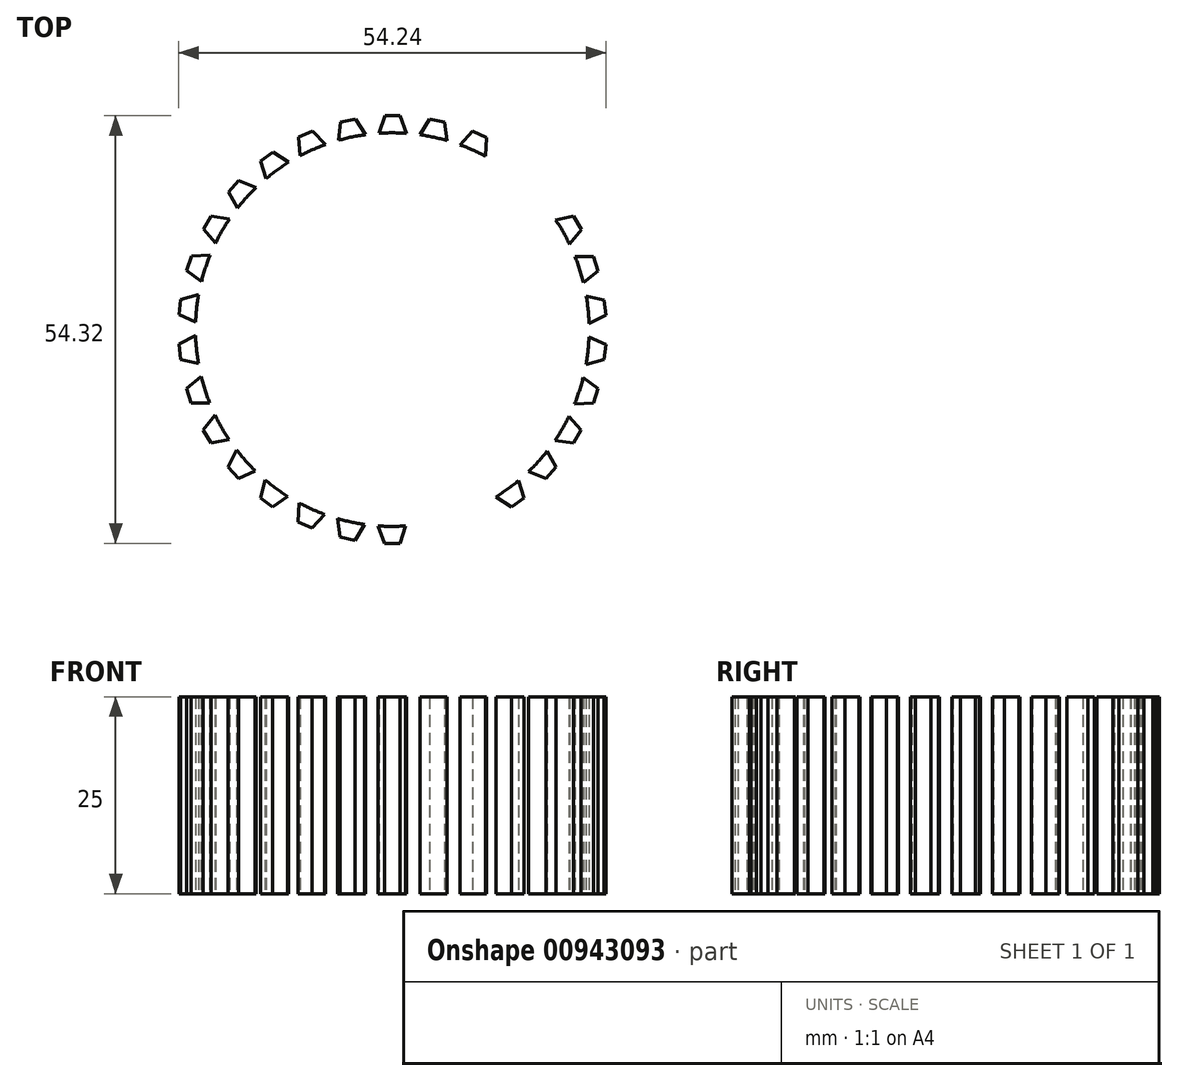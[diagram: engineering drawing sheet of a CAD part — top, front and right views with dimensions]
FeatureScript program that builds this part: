
annotation { "Feature Type Name" : "Feature", "Feature Type Description" : "" }
export const myFeature = defineFeature(function(context is Context, id is Id, definition is map)
    precondition{}
    {
        {
            var Q0;
            Q0=qCreatedBy(makeId("Top.planeOp"),FACE);
            var sketch = newSketch(context, id + "F0", { "sketchPlane" : qUnion([Q0])});
            skCircle(sketch, "E0", {"center": v(0, 0) * mm, "radius": 25 * mm});
            skLineSegment(sketch, "E1", {"start": v(0, 0) * mm, "end": v(0, 25) * mm});
            skLineSegment(sketch, "E2", {"start": v(-1.69, 24.94) * mm, "end": v(-0.95, 27.16) * mm});
            skLineSegment(sketch, "E3", {"start": v(-0.95, 27.16) * mm, "end": v(0.98, 27.16) * mm});
            skLineSegment(sketch, "E4", {"start": v(0.98, 27.16) * mm, "end": v(1.84, 24.93) * mm});
            skLineSegment(sketch, "E5.1.0", {"start": v(-6.83, 24.05) * mm, "end": v(-6.58, 26.37) * mm});
            skLineSegment(sketch, "E5.1.1", {"start": v(-6.58, 26.37) * mm, "end": v(-4.68, 26.77) * mm});
            skLineSegment(sketch, "E5.1.2", {"start": v(-4.68, 26.77) * mm, "end": v(-3.39, 24.77) * mm});
            skLineSegment(sketch, "E5.2.0", {"start": v(-11.69, 22.1) * mm, "end": v(-11.92, 24.43) * mm});
            skLineSegment(sketch, "E5.2.1", {"start": v(-11.92, 24.43) * mm, "end": v(-10.15, 25.21) * mm});
            skLineSegment(sketch, "E5.2.2", {"start": v(-10.15, 25.21) * mm, "end": v(-8.46, 23.52) * mm});
            skLineSegment(sketch, "E5.3.0", {"start": v(-16.02, 19.19) * mm, "end": v(-16.74, 21.41) * mm});
            skLineSegment(sketch, "E5.3.1", {"start": v(-16.74, 21.41) * mm, "end": v(-15.17, 22.55) * mm});
            skLineSegment(sketch, "E5.3.2", {"start": v(-15.17, 22.55) * mm, "end": v(-13.17, 21.25) * mm});
            skLineSegment(sketch, "E5.4.0", {"start": v(-19.66, 15.44) * mm, "end": v(-20.82, 17.47) * mm});
            skLineSegment(sketch, "E5.4.1", {"start": v(-20.82, 17.47) * mm, "end": v(-19.53, 18.9) * mm});
            skLineSegment(sketch, "E5.4.2", {"start": v(-19.53, 18.9) * mm, "end": v(-17.3, 18.05) * mm});
            skLineSegment(sketch, "E5.5.0", {"start": v(-22.44, 11.01) * mm, "end": v(-24, 12.76) * mm});
            skLineSegment(sketch, "E5.5.1", {"start": v(-24, 12.76) * mm, "end": v(-23.03, 14.43) * mm});
            skLineSegment(sketch, "E5.5.2", {"start": v(-23.03, 14.43) * mm, "end": v(-20.67, 14.06) * mm});
            skLineSegment(sketch, "E5.6.0", {"start": v(-24.24, 6.1) * mm, "end": v(-26.13, 7.49) * mm});
            skLineSegment(sketch, "E5.6.1", {"start": v(-26.13, 7.49) * mm, "end": v(-25.53, 9.33) * mm});
            skLineSegment(sketch, "E5.6.2", {"start": v(-25.53, 9.33) * mm, "end": v(-23.14, 9.45) * mm});
            skLineSegment(sketch, "E5.7.0", {"start": v(-24.98, 0.93) * mm, "end": v(-27.11, 1.9) * mm});
            skLineSegment(sketch, "E5.7.1", {"start": v(-27.11, 1.9) * mm, "end": v(-26.91, 3.82) * mm});
            skLineSegment(sketch, "E5.7.2", {"start": v(-26.91, 3.82) * mm, "end": v(-24.6, 4.43) * mm});
            skLineSegment(sketch, "E5.8.0", {"start": v(-24.63, -4.28) * mm, "end": v(-26.91, -3.79) * mm});
            skLineSegment(sketch, "E5.8.1", {"start": v(-26.91, -3.79) * mm, "end": v(-27.12, -1.86) * mm});
            skLineSegment(sketch, "E5.8.2", {"start": v(-27.12, -1.86) * mm, "end": v(-24.99, -0.78) * mm});
            skLineSegment(sketch, "E5.9.0", {"start": v(-23.2, -9.31) * mm, "end": v(-25.54, -9.3) * mm});
            skLineSegment(sketch, "E5.9.1", {"start": v(-25.54, -9.3) * mm, "end": v(-26.14, -7.46) * mm});
            skLineSegment(sketch, "E5.9.2", {"start": v(-26.14, -7.46) * mm, "end": v(-24.28, -5.96) * mm});
            skLineSegment(sketch, "E5.10.0", {"start": v(-20.76, -13.93) * mm, "end": v(-23.05, -14.4) * mm});
            skLineSegment(sketch, "E5.10.1", {"start": v(-23.05, -14.4) * mm, "end": v(-24.02, -12.73) * mm});
            skLineSegment(sketch, "E5.10.2", {"start": v(-24.02, -12.73) * mm, "end": v(-22.51, -10.87) * mm});
            skLineSegment(sketch, "E5.11.0", {"start": v(-17.4, -17.94) * mm, "end": v(-19.55, -18.88) * mm});
            skLineSegment(sketch, "E5.11.1", {"start": v(-19.55, -18.88) * mm, "end": v(-20.84, -17.44) * mm});
            skLineSegment(sketch, "E5.11.2", {"start": v(-20.84, -17.44) * mm, "end": v(-19.76, -15.32) * mm});
            skLineSegment(sketch, "E5.12.0", {"start": v(-13.3, -21.17) * mm, "end": v(-15.2, -22.53) * mm});
            skLineSegment(sketch, "E5.12.1", {"start": v(-15.2, -22.53) * mm, "end": v(-16.76, -21.4) * mm});
            skLineSegment(sketch, "E5.12.2", {"start": v(-16.76, -21.4) * mm, "end": v(-16.14, -19.1) * mm});
            skLineSegment(sketch, "E5.13.0", {"start": v(-8.6, -23.47) * mm, "end": v(-10.18, -25.2) * mm});
            skLineSegment(sketch, "E5.13.1", {"start": v(-10.18, -25.2) * mm, "end": v(-11.95, -24.41) * mm});
            skLineSegment(sketch, "E5.13.2", {"start": v(-11.95, -24.41) * mm, "end": v(-11.82, -22.03) * mm});
            skLineSegment(sketch, "E5.14.0", {"start": v(-3.54, -24.75) * mm, "end": v(-4.72, -26.77) * mm});
            skLineSegment(sketch, "E5.14.1", {"start": v(-4.72, -26.77) * mm, "end": v(-6.61, -26.36) * mm});
            skLineSegment(sketch, "E5.14.2", {"start": v(-6.61, -26.36) * mm, "end": v(-6.98, -24) * mm});
            skLineSegment(sketch, "E5.15.0", {"start": v(1.69, -24.94) * mm, "end": v(0.95, -27.16) * mm});
            skLineSegment(sketch, "E5.15.1", {"start": v(0.95, -27.16) * mm, "end": v(-0.98, -27.16) * mm});
            skLineSegment(sketch, "E5.15.2", {"start": v(-0.98, -27.16) * mm, "end": v(-1.84, -24.93) * mm});
            skLineSegment(sketch, "E5.16.0", {"start": v(6.83, -24.05) * mm, "end": v(6.58, -26.37) * mm});
            skLineSegment(sketch, "E5.16.1", {"start": v(6.58, -26.37) * mm, "end": v(4.68, -26.77) * mm});
            skLineSegment(sketch, "E5.16.2", {"start": v(4.68, -26.77) * mm, "end": v(3.39, -24.77) * mm});
            skLineSegment(sketch, "E5.17.0", {"start": v(11.69, -22.1) * mm, "end": v(11.92, -24.43) * mm});
            skLineSegment(sketch, "E5.17.1", {"start": v(11.92, -24.43) * mm, "end": v(10.15, -25.21) * mm});
            skLineSegment(sketch, "E5.17.2", {"start": v(10.15, -25.21) * mm, "end": v(8.46, -23.52) * mm});
            skLineSegment(sketch, "E5.18.0", {"start": v(16.02, -19.19) * mm, "end": v(16.74, -21.41) * mm});
            skLineSegment(sketch, "E5.18.1", {"start": v(16.74, -21.41) * mm, "end": v(15.17, -22.55) * mm});
            skLineSegment(sketch, "E5.18.2", {"start": v(15.17, -22.55) * mm, "end": v(13.17, -21.25) * mm});
            skLineSegment(sketch, "E5.19.0", {"start": v(19.66, -15.44) * mm, "end": v(20.82, -17.47) * mm});
            skLineSegment(sketch, "E5.19.1", {"start": v(20.82, -17.47) * mm, "end": v(19.53, -18.9) * mm});
            skLineSegment(sketch, "E5.19.2", {"start": v(19.53, -18.9) * mm, "end": v(17.3, -18.05) * mm});
            skLineSegment(sketch, "E5.20.0", {"start": v(22.44, -11.01) * mm, "end": v(24, -12.76) * mm});
            skLineSegment(sketch, "E5.20.1", {"start": v(24, -12.76) * mm, "end": v(23.03, -14.43) * mm});
            skLineSegment(sketch, "E5.20.2", {"start": v(23.03, -14.43) * mm, "end": v(20.67, -14.06) * mm});
            skLineSegment(sketch, "E5.21.0", {"start": v(24.24, -6.1) * mm, "end": v(26.13, -7.49) * mm});
            skLineSegment(sketch, "E5.21.1", {"start": v(26.13, -7.49) * mm, "end": v(25.53, -9.33) * mm});
            skLineSegment(sketch, "E5.21.2", {"start": v(25.53, -9.33) * mm, "end": v(23.14, -9.45) * mm});
            skLineSegment(sketch, "E5.22.0", {"start": v(24.98, -0.93) * mm, "end": v(27.11, -1.9) * mm});
            skLineSegment(sketch, "E5.22.1", {"start": v(27.11, -1.9) * mm, "end": v(26.91, -3.82) * mm});
            skLineSegment(sketch, "E5.22.2", {"start": v(26.91, -3.82) * mm, "end": v(24.6, -4.43) * mm});
            skLineSegment(sketch, "E5.23.0", {"start": v(24.63, 4.28) * mm, "end": v(26.91, 3.79) * mm});
            skLineSegment(sketch, "E5.23.1", {"start": v(26.91, 3.79) * mm, "end": v(27.12, 1.86) * mm});
            skLineSegment(sketch, "E5.23.2", {"start": v(27.12, 1.86) * mm, "end": v(24.99, 0.78) * mm});
            skLineSegment(sketch, "E5.24.0", {"start": v(23.2, 9.31) * mm, "end": v(25.54, 9.3) * mm});
            skLineSegment(sketch, "E5.24.1", {"start": v(25.54, 9.3) * mm, "end": v(26.14, 7.46) * mm});
            skLineSegment(sketch, "E5.24.2", {"start": v(26.14, 7.46) * mm, "end": v(24.28, 5.96) * mm});
            skLineSegment(sketch, "E5.25.0", {"start": v(20.76, 13.93) * mm, "end": v(23.05, 14.4) * mm});
            skLineSegment(sketch, "E5.25.1", {"start": v(23.05, 14.4) * mm, "end": v(24.02, 12.73) * mm});
            skLineSegment(sketch, "E5.25.2", {"start": v(24.02, 12.73) * mm, "end": v(22.51, 10.87) * mm});
            skLineSegment(sketch, "E5.26.0", {"start": v(17.4, 17.94) * mm, "end": v(19.55, 18.88) * mm});
            skLineSegment(sketch, "E5.26.1", {"start": v(19.55, 18.88) * mm, "end": v(20.84, 17.44) * mm});
            skLineSegment(sketch, "E5.26.2", {"start": v(20.84, 17.44) * mm, "end": v(19.76, 15.32) * mm});
            skLineSegment(sketch, "E5.27.0", {"start": v(13.3, 21.17) * mm, "end": v(15.2, 22.53) * mm});
            skLineSegment(sketch, "E5.27.1", {"start": v(15.2, 22.53) * mm, "end": v(16.76, 21.4) * mm});
            skLineSegment(sketch, "E5.27.2", {"start": v(16.76, 21.4) * mm, "end": v(16.14, 19.1) * mm});
            skLineSegment(sketch, "E5.28.0", {"start": v(8.6, 23.47) * mm, "end": v(10.18, 25.2) * mm});
            skLineSegment(sketch, "E5.28.1", {"start": v(10.18, 25.2) * mm, "end": v(11.95, 24.41) * mm});
            skLineSegment(sketch, "E5.28.2", {"start": v(11.95, 24.41) * mm, "end": v(11.82, 22.03) * mm});
            skLineSegment(sketch, "E5.29.0", {"start": v(3.54, 24.75) * mm, "end": v(4.72, 26.77) * mm});
            skLineSegment(sketch, "E5.29.1", {"start": v(4.72, 26.77) * mm, "end": v(6.61, 26.36) * mm});
            skLineSegment(sketch, "E5.29.2", {"start": v(6.61, 26.36) * mm, "end": v(6.98, 24) * mm});
            skSolve(sketch);
        }
        {
            var Q0;
            {var subQ0=sQuery(id+"F0.wireOp",EDGE,"E0");var subQ56=makeQuery(id+"F0.imprint","IMPRINT",VERTEX,{"derivedFrom":subQ0});Q0=makeQuery(id+"F0.imprint","IMPRINT",FACE,{"disambiguationData":[TD([[makeQuery(id+"F0.imprint","IMPRINT",EDGE,{"disambiguationData":[TD([[subQ56,1.0]])],"derivedFrom":subQ0}),-1.0]])]});}
            var Q1;
            {var subQ3=sQuery(id+"F0.wireOp",EDGE,"E2");Q1=makeQuery(id+"F0.imprint","IMPRINT",FACE,{"disambiguationData":[TD([[makeQuery(id+"F0.imprint","IMPRINT",EDGE,{"derivedFrom":subQ3}),-1.0]])]});}
            var Q2;
            {var subQ0=sQuery(id+"F0.wireOp",EDGE,"E5.19.0");Q2=makeQuery(id+"F0.imprint","IMPRINT",FACE,{"disambiguationData":[TD([[makeQuery(id+"F0.imprint","IMPRINT",EDGE,{"derivedFrom":subQ0}),-1.0]])]});}
            var Q3;
            {var subQ0=sQuery(id+"F0.wireOp",EDGE,"E5.21.0");Q3=makeQuery(id+"F0.imprint","IMPRINT",FACE,{"disambiguationData":[TD([[makeQuery(id+"F0.imprint","IMPRINT",EDGE,{"derivedFrom":subQ0}),-1.0]])]});}
            var Q4;
            {var subQ0=sQuery(id+"F0.wireOp",EDGE,"E5.29.0");Q4=makeQuery(id+"F0.imprint","IMPRINT",FACE,{"disambiguationData":[TD([[makeQuery(id+"F0.imprint","IMPRINT",EDGE,{"derivedFrom":subQ0}),-1.0]])]});}
            var Q5;
            {var subQ0=sQuery(id+"F0.wireOp",EDGE,"E5.1.0");Q5=makeQuery(id+"F0.imprint","IMPRINT",FACE,{"disambiguationData":[TD([[makeQuery(id+"F0.imprint","IMPRINT",EDGE,{"derivedFrom":subQ0}),-1.0]])]});}
            var Q6;
            {var subQ0=sQuery(id+"F0.wireOp",EDGE,"E5.2.0");Q6=makeQuery(id+"F0.imprint","IMPRINT",FACE,{"disambiguationData":[TD([[makeQuery(id+"F0.imprint","IMPRINT",EDGE,{"derivedFrom":subQ0}),-1.0]])]});}
            var Q7;
            Q7=makeQuery(id+"F0.imprint","IMPRINT",FACE,{"disambiguationData":[TD([[makeQuery(id+"F0.imprint","IMPRINT",EDGE,{"derivedFrom":sQuery(id+"F0.wireOp",EDGE,"E5.26.1")}),-1.0]])]});
            var Q8;
            {var subQ0=sQuery(id+"F0.wireOp",EDGE,"E5.20.0");Q8=makeQuery(id+"F0.imprint","IMPRINT",FACE,{"disambiguationData":[TD([[makeQuery(id+"F0.imprint","IMPRINT",EDGE,{"derivedFrom":subQ0}),-1.0]])]});}
            var Q9;
            {var subQ0=sQuery(id+"F0.wireOp",EDGE,"E5.22.0");Q9=makeQuery(id+"F0.imprint","IMPRINT",FACE,{"disambiguationData":[TD([[makeQuery(id+"F0.imprint","IMPRINT",EDGE,{"derivedFrom":subQ0}),-1.0]])]});}
            var Q10;
            {var subQ0=sQuery(id+"F0.wireOp",EDGE,"E5.23.0");Q10=makeQuery(id+"F0.imprint","IMPRINT",FACE,{"disambiguationData":[TD([[makeQuery(id+"F0.imprint","IMPRINT",EDGE,{"derivedFrom":subQ0}),-1.0]])]});}
            var Q11;
            {var subQ0=sQuery(id+"F0.wireOp",EDGE,"E5.24.0");Q11=makeQuery(id+"F0.imprint","IMPRINT",FACE,{"disambiguationData":[TD([[makeQuery(id+"F0.imprint","IMPRINT",EDGE,{"derivedFrom":subQ0}),-1.0]])]});}
            var Q12;
            {var subQ0=sQuery(id+"F0.wireOp",EDGE,"E5.28.0");Q12=makeQuery(id+"F0.imprint","IMPRINT",FACE,{"disambiguationData":[TD([[makeQuery(id+"F0.imprint","IMPRINT",EDGE,{"derivedFrom":subQ0}),-1.0]])]});}
            var Q13;
            {var subQ0=sQuery(id+"F0.wireOp",EDGE,"E5.27.0");Q13=makeQuery(id+"F0.imprint","IMPRINT",FACE,{"disambiguationData":[TD([[makeQuery(id+"F0.imprint","IMPRINT",EDGE,{"derivedFrom":subQ0}),-1.0]])]});}
            var Q14;
            {var subQ0=sQuery(id+"F0.wireOp",EDGE,"E5.25.2");Q14=makeQuery(id+"F0.imprint","IMPRINT",FACE,{"disambiguationData":[TD([[makeQuery(id+"F0.imprint","IMPRINT",EDGE,{"derivedFrom":subQ0}),-1.0]])]});}
            var Q15;
            {var subQ0=sQuery(id+"F0.wireOp",EDGE,"E5.13.0");Q15=makeQuery(id+"F0.imprint","IMPRINT",FACE,{"disambiguationData":[TD([[makeQuery(id+"F0.imprint","IMPRINT",EDGE,{"derivedFrom":subQ0}),-1.0]])]});}
            var Q16;
            {var subQ0=sQuery(id+"F0.wireOp",EDGE,"E5.14.0");Q16=makeQuery(id+"F0.imprint","IMPRINT",FACE,{"disambiguationData":[TD([[makeQuery(id+"F0.imprint","IMPRINT",EDGE,{"derivedFrom":subQ0}),-1.0]])]});}
            var Q17;
            {var subQ0=sQuery(id+"F0.wireOp",EDGE,"E5.5.0");Q17=makeQuery(id+"F0.imprint","IMPRINT",FACE,{"disambiguationData":[TD([[makeQuery(id+"F0.imprint","IMPRINT",EDGE,{"derivedFrom":subQ0}),-1.0]])]});}
            var Q18;
            {var subQ0=sQuery(id+"F0.wireOp",EDGE,"E5.11.0");Q18=makeQuery(id+"F0.imprint","IMPRINT",FACE,{"disambiguationData":[TD([[makeQuery(id+"F0.imprint","IMPRINT",EDGE,{"derivedFrom":subQ0}),-1.0]])]});}
            var Q19;
            {var subQ0=sQuery(id+"F0.wireOp",EDGE,"E5.12.0");Q19=makeQuery(id+"F0.imprint","IMPRINT",FACE,{"disambiguationData":[TD([[makeQuery(id+"F0.imprint","IMPRINT",EDGE,{"derivedFrom":subQ0}),-1.0]])]});}
            var Q20;
            Q20=makeQuery(id+"F0.imprint","IMPRINT",FACE,{"disambiguationData":[TD([[makeQuery(id+"F0.imprint","IMPRINT",EDGE,{"derivedFrom":sQuery(id+"F0.wireOp",EDGE,"E5.16.1")}),-1.0]])]});
            var Q21;
            {var subQ0=sQuery(id+"F0.wireOp",EDGE,"E5.3.0");Q21=makeQuery(id+"F0.imprint","IMPRINT",FACE,{"disambiguationData":[TD([[makeQuery(id+"F0.imprint","IMPRINT",EDGE,{"derivedFrom":subQ0}),-1.0]])]});}
            var Q22;
            {var subQ0=sQuery(id+"F0.wireOp",EDGE,"E5.4.0");Q22=makeQuery(id+"F0.imprint","IMPRINT",FACE,{"disambiguationData":[TD([[makeQuery(id+"F0.imprint","IMPRINT",EDGE,{"derivedFrom":subQ0}),-1.0]])]});}
            var Q23;
            {var subQ0=sQuery(id+"F0.wireOp",EDGE,"E5.6.0");Q23=makeQuery(id+"F0.imprint","IMPRINT",FACE,{"disambiguationData":[TD([[makeQuery(id+"F0.imprint","IMPRINT",EDGE,{"derivedFrom":subQ0}),-1.0]])]});}
            var Q24;
            {var subQ0=sQuery(id+"F0.wireOp",EDGE,"E5.7.0");Q24=makeQuery(id+"F0.imprint","IMPRINT",FACE,{"disambiguationData":[TD([[makeQuery(id+"F0.imprint","IMPRINT",EDGE,{"derivedFrom":subQ0}),-1.0]])]});}
            var Q25;
            {var subQ0=sQuery(id+"F0.wireOp",EDGE,"E5.8.0");Q25=makeQuery(id+"F0.imprint","IMPRINT",FACE,{"disambiguationData":[TD([[makeQuery(id+"F0.imprint","IMPRINT",EDGE,{"derivedFrom":subQ0}),-1.0]])]});}
            var Q26;
            {var subQ0=sQuery(id+"F0.wireOp",EDGE,"E5.9.0");Q26=makeQuery(id+"F0.imprint","IMPRINT",FACE,{"disambiguationData":[TD([[makeQuery(id+"F0.imprint","IMPRINT",EDGE,{"derivedFrom":subQ0}),-1.0]])]});}
            var Q27;
            {var subQ0=sQuery(id+"F0.wireOp",EDGE,"E5.10.0");Q27=makeQuery(id+"F0.imprint","IMPRINT",FACE,{"disambiguationData":[TD([[makeQuery(id+"F0.imprint","IMPRINT",EDGE,{"derivedFrom":subQ0}),-1.0]])]});}
            var Q28;
            {var subQ0=sQuery(id+"F0.wireOp",EDGE,"E5.18.0");Q28=makeQuery(id+"F0.imprint","IMPRINT",FACE,{"disambiguationData":[TD([[makeQuery(id+"F0.imprint","IMPRINT",EDGE,{"derivedFrom":subQ0}),-1.0]])]});}
            var Q29;
            {var subQ0=sQuery(id+"F0.wireOp",EDGE,"E5.15.2");Q29=makeQuery(id+"F0.imprint","IMPRINT",FACE,{"disambiguationData":[TD([[makeQuery(id+"F0.imprint","IMPRINT",EDGE,{"derivedFrom":subQ0}),-1.0]])]});}
            var Q30;
            {var subQ0=sQuery(id+"F0.wireOp",EDGE,"E5.17.0");Q30=makeQuery(id+"F0.imprint","IMPRINT",FACE,{"disambiguationData":[TD([[makeQuery(id+"F0.imprint","IMPRINT",EDGE,{"derivedFrom":subQ0}),-1.0]])]});}
            extrude(context, id + "F1", {"entities" : qUnion([Q0, Q1, Q2, Q3, Q4, Q5, Q6, Q7, Q8, Q9, Q10, Q11, Q12, Q13, Q14, Q15, Q16, Q17, Q18, Q19, Q20, Q21, Q22, Q23, Q24, Q25, Q26, Q27, Q28, Q29, Q30]), "depth" : 25 * mm, "offsetDistance" : 25 * mm});
        }
        {
            var Q0;
            Q0=makeQuery(id+"F1.opExtrude","CAP_FACE",FACE,{"disambiguationData":[OSD([sQuery(id+"F0.wireOp",EDGE,"E2"),sQuery(id+"F0.wireOp",EDGE,"E3"),sQuery(id+"F0.wireOp",EDGE,"E4"),sQuery(id+"F0.wireOp",EDGE,"E5.1.0"),sQuery(id+"F0.wireOp",EDGE,"E5.1.1"),sQuery(id+"F0.wireOp",EDGE,"E5.1.2"),sQuery(id+"F0.wireOp",EDGE,"E5.2.0"),sQuery(id+"F0.wireOp",EDGE,"E5.2.1"),sQuery(id+"F0.wireOp",EDGE,"E5.2.2"),sQuery(id+"F0.wireOp",EDGE,"E5.3.0"),sQuery(id+"F0.wireOp",EDGE,"E5.3.1"),sQuery(id+"F0.wireOp",EDGE,"E5.3.2"),sQuery(id+"F0.wireOp",EDGE,"E5.4.0"),sQuery(id+"F0.wireOp",EDGE,"E5.4.1"),sQuery(id+"F0.wireOp",EDGE,"E5.4.2"),sQuery(id+"F0.wireOp",EDGE,"E5.5.0"),sQuery(id+"F0.wireOp",EDGE,"E5.5.1"),sQuery(id+"F0.wireOp",EDGE,"E5.5.2"),sQuery(id+"F0.wireOp",EDGE,"E5.6.0"),sQuery(id+"F0.wireOp",EDGE,"E5.6.1"),sQuery(id+"F0.wireOp",EDGE,"E5.6.2"),sQuery(id+"F0.wireOp",EDGE,"E5.7.0"),sQuery(id+"F0.wireOp",EDGE,"E5.7.1"),sQuery(id+"F0.wireOp",EDGE,"E5.7.2"),sQuery(id+"F0.wireOp",EDGE,"E5.8.0"),sQuery(id+"F0.wireOp",EDGE,"E5.8.1"),sQuery(id+"F0.wireOp",EDGE,"E5.8.2"),sQuery(id+"F0.wireOp",EDGE,"E5.9.0"),sQuery(id+"F0.wireOp",EDGE,"E5.9.1"),sQuery(id+"F0.wireOp",EDGE,"E5.9.2"),sQuery(id+"F0.wireOp",EDGE,"E5.10.0"),sQuery(id+"F0.wireOp",EDGE,"E5.10.1"),sQuery(id+"F0.wireOp",EDGE,"E5.10.2"),sQuery(id+"F0.wireOp",EDGE,"E5.11.0"),sQuery(id+"F0.wireOp",EDGE,"E5.11.1"),sQuery(id+"F0.wireOp",EDGE,"E5.11.2"),sQuery(id+"F0.wireOp",EDGE,"E5.12.0"),sQuery(id+"F0.wireOp",EDGE,"E5.12.1"),sQuery(id+"F0.wireOp",EDGE,"E5.12.2"),sQuery(id+"F0.wireOp",EDGE,"E5.13.0"),sQuery(id+"F0.wireOp",EDGE,"E5.13.1"),sQuery(id+"F0.wireOp",EDGE,"E5.13.2"),sQuery(id+"F0.wireOp",EDGE,"E5.14.0"),sQuery(id+"F0.wireOp",EDGE,"E5.14.1"),sQuery(id+"F0.wireOp",EDGE,"E5.14.2"),sQuery(id+"F0.wireOp",EDGE,"E5.15.2"),sQuery(id+"F0.wireOp",EDGE,"E5.18.0"),sQuery(id+"F0.wireOp",EDGE,"E5.18.1"),sQuery(id+"F0.wireOp",EDGE,"E5.18.2"),sQuery(id+"F0.wireOp",EDGE,"E5.19.0"),sQuery(id+"F0.wireOp",EDGE,"E5.19.1"),sQuery(id+"F0.wireOp",EDGE,"E5.19.2"),sQuery(id+"F0.wireOp",EDGE,"E5.20.0"),sQuery(id+"F0.wireOp",EDGE,"E5.20.1"),sQuery(id+"F0.wireOp",EDGE,"E5.20.2"),sQuery(id+"F0.wireOp",EDGE,"E5.21.0"),sQuery(id+"F0.wireOp",EDGE,"E5.21.1"),sQuery(id+"F0.wireOp",EDGE,"E5.21.2"),sQuery(id+"F0.wireOp",EDGE,"E5.22.0"),sQuery(id+"F0.wireOp",EDGE,"E5.22.1"),sQuery(id+"F0.wireOp",EDGE,"E5.22.2"),sQuery(id+"F0.wireOp",EDGE,"E5.23.0"),sQuery(id+"F0.wireOp",EDGE,"E5.23.1"),sQuery(id+"F0.wireOp",EDGE,"E5.23.2"),sQuery(id+"F0.wireOp",EDGE,"E5.24.0"),sQuery(id+"F0.wireOp",EDGE,"E5.24.1"),sQuery(id+"F0.wireOp",EDGE,"E5.24.2"),sQuery(id+"F0.wireOp",EDGE,"E5.25.2"),sQuery(id+"F0.wireOp",EDGE,"E5.28.0"),sQuery(id+"F0.wireOp",EDGE,"E5.28.1"),sQuery(id+"F0.wireOp",EDGE,"E5.28.2"),sQuery(id+"F0.wireOp",EDGE,"E5.29.0"),sQuery(id+"F0.wireOp",EDGE,"E5.29.1"),sQuery(id+"F0.wireOp",EDGE,"E5.29.2"),sQuery(id+"F0.wireOp",EDGE,"E5.17.0"),sQuery(id+"F0.wireOp",EDGE,"E5.17.2"),sQuery(id+"F0.wireOp",EDGE,"E5.17.1"),sQuery(id+"F0.wireOp",EDGE,"E5.16.1"),sQuery(id+"F0.wireOp",EDGE,"E5.16.0"),sQuery(id+"F0.wireOp",EDGE,"E5.16.2"),sQuery(id+"F0.wireOp",EDGE,"E5.15.0"),sQuery(id+"F0.wireOp",EDGE,"E5.15.1"),sQuery(id+"F0.wireOp",EDGE,"E0"),sQuery(id+"F0.wireOp",EDGE,"E5.27.0"),sQuery(id+"F0.wireOp",EDGE,"E5.27.2"),sQuery(id+"F0.wireOp",EDGE,"E5.27.1"),sQuery(id+"F0.wireOp",EDGE,"E5.26.1"),sQuery(id+"F0.wireOp",EDGE,"E5.26.0"),sQuery(id+"F0.wireOp",EDGE,"E5.26.2"),sQuery(id+"F0.wireOp",EDGE,"E5.25.0"),sQuery(id+"F0.wireOp",EDGE,"E5.25.1")])],"isStart":true});
            var sketch = newSketch(context, id + "F2", { "sketchPlane" : qUnion([Q0])});
            skCircle(sketch, "E6", {"center": v(0, 0) * mm, "radius": 5.63 * mm});
            skSolve(sketch);
        }
        {
            var Q0;
            Q0 = qSketchRegion(id + "F2", true);
            extrude(context, id + "F3", {"entities" : qUnion([Q0]), "operationType" : NewBodyOperationType.REMOVE, "endBound" : BoundingType.THROUGH_ALL, "oppositeDirection" : true, "depth" : 25 * mm, "offsetDistance" : 25 * mm});
        }
    });
